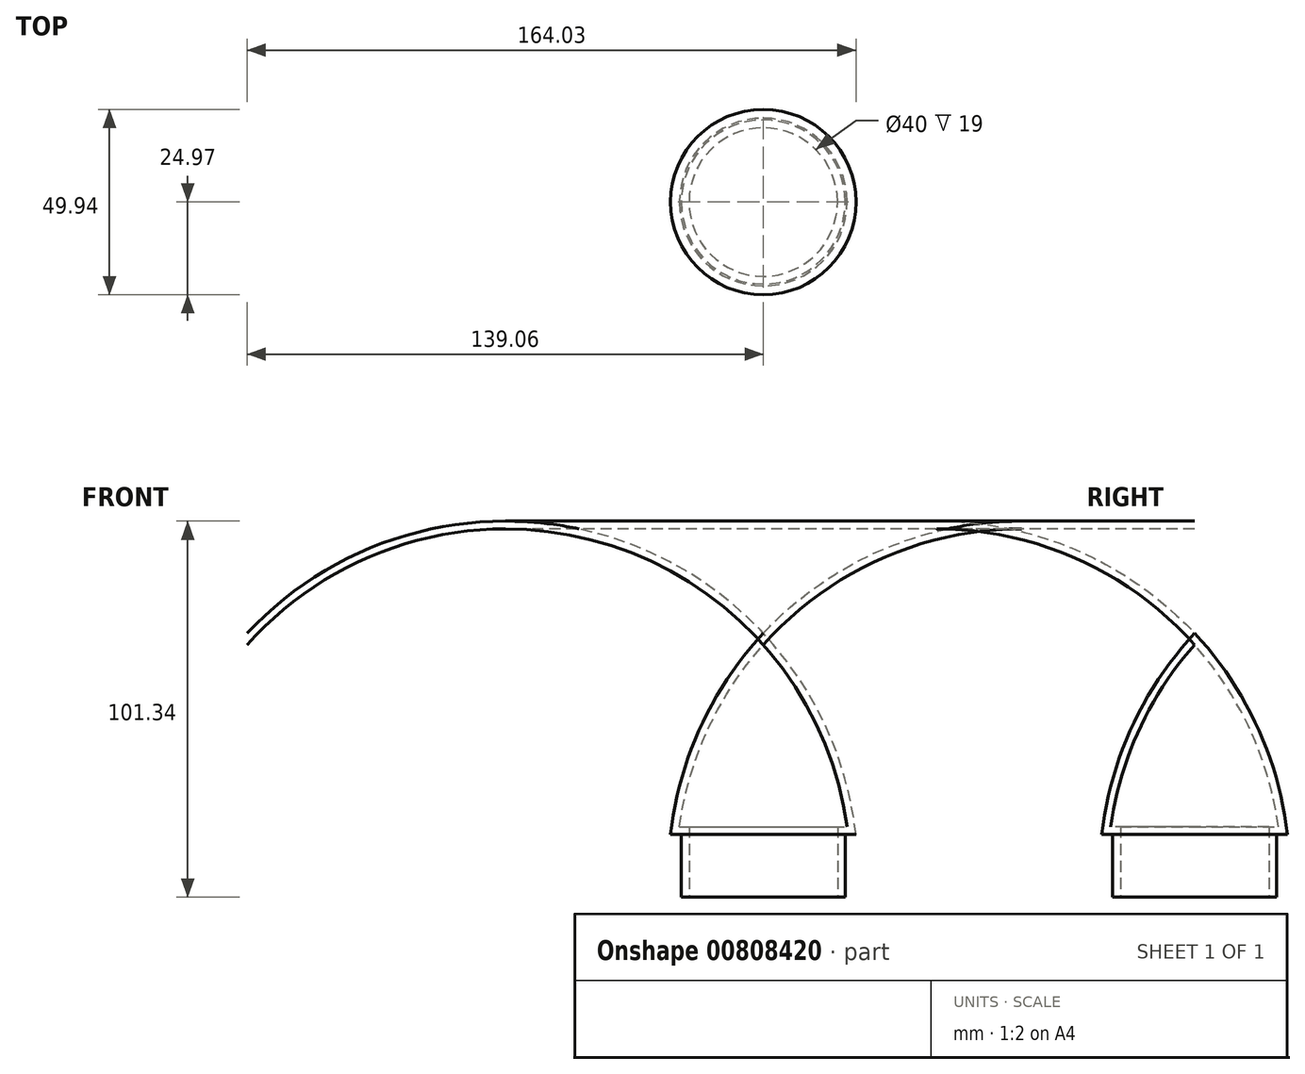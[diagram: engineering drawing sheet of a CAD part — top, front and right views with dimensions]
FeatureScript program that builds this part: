
annotation { "Feature Type Name" : "Feature", "Feature Type Description" : "" }
export const myFeature = defineFeature(function(context is Context, id is Id, definition is map)
    precondition{}
    {
        {
            var Q0;
            Q0=qCreatedBy(makeId("Front.planeOp"),FACE);
            var sketch = newSketch(context, id + "F0", { "sketchPlane" : qUnion([Q0])});
            skLineSegment(sketch, "E0", {"start": v(0, 0) * mm, "end": v(0, 68) * mm});
            skLineSegment(sketch, "E1", {"start": v(20, 0) * mm, "end": v(20, 19) * mm});
            skArc(sketch, "E2", {"start": v(22.6, 19) * mm, "mid": v(14.93, 45.17) * mm, "end": v(0, 68) * mm});
            skLineSegment(sketch, "E3", {"start": v(20, 19) * mm, "end": v(22.6, 19) * mm});
            skArc(sketch, "E4.0", {"start": v(24.97, 16.9) * mm, "mid": v(16.85, 46.02) * mm, "end": v(0, 71.12) * mm});
            skLineSegment(sketch, "E4.1", {"start": v(22.1, 16.9) * mm, "end": v(24.97, 16.9) * mm});
            skLineSegment(sketch, "E4.2", {"start": v(22.1, 0) * mm, "end": v(22.1, 16.9) * mm});
            skLineSegment(sketch, "E5", {"start": v(20, 0) * mm, "end": v(22.1, 0) * mm});
            skLineSegment(sketch, "E6", {"start": v(0, 68) * mm, "end": v(0, 71.12) * mm});
            skSolve(sketch);
        }
        {
            var Q0;
            Q0=makeQuery(id+"F0.imprint","IMPRINT",FACE,{"disambiguationData":[TD([[makeQuery(id+"F0.imprint","IMPRINT",EDGE,{"derivedFrom":sQuery(id+"F0.wireOp",EDGE,"E1")}),-1.0]])]});
            var Q1;
            Q1=sQuery(id+"F0.wireOp",EDGE,"E0");
            revolve(context, id + "F1", {"surfaceOperationType" : NewSurfaceOperationType.NEW, "entities" : qUnion([Q0]), "axis" : qUnion([Q1]), "revolveType" : RevolveType.FULL});
        }
    });
